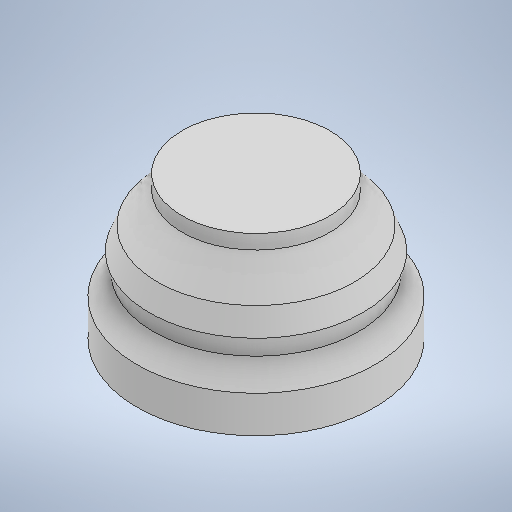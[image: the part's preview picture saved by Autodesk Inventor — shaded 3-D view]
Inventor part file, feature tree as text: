
AUTODESK INVENTOR PART (.ipt)
format: ipt  version: 2025.1 (Build 291241000, 241)  size: 293,376 bytes
history: native  units: mm
features: other x2, revolve x1, sketch x1
ambient origin geometry x8: Origin, YZ Plane, XZ Plane, XY Plane, X Axis, Y Axis, Z Axis, Center Point
bodies: Body1 (feature_tree)
feature tree (4):
  other  "Sólido1"
  revolve  "Revolución1"  [1 undecoded]
  sketch  "Boceto2"  dims[d16=90.0deg]
  other  "Imagen2"
note: 1 required parameter value undecoded (feature->parameter linkage not recoverable at this tier; creation-order binding heuristic only, values carry confidence <= 0.55)
